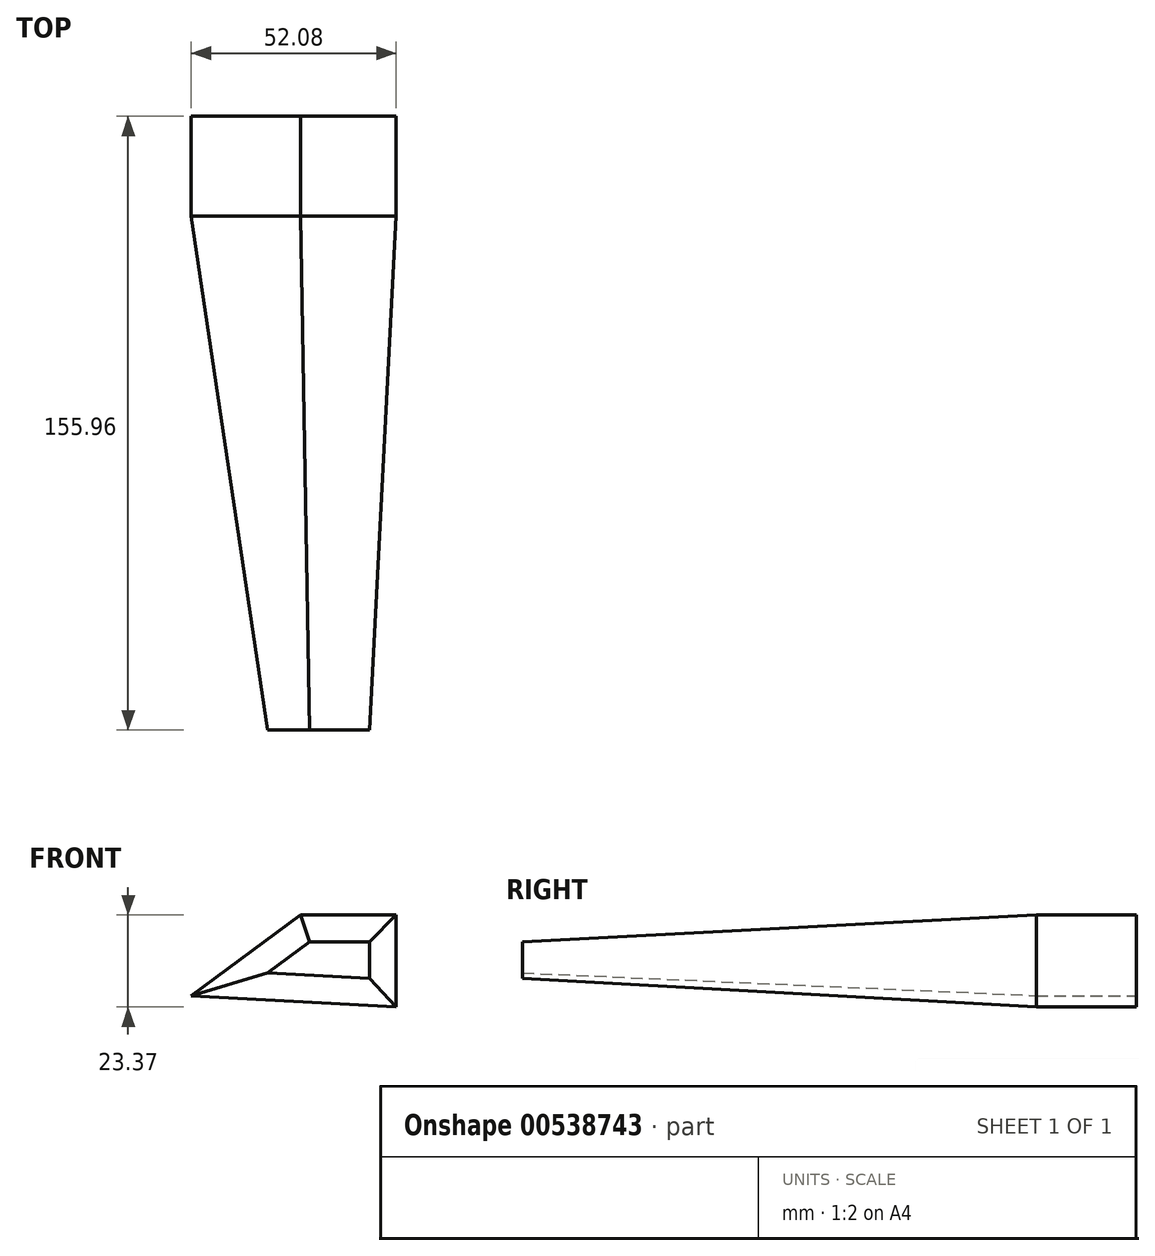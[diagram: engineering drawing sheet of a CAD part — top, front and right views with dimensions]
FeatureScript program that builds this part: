
annotation { "Feature Type Name" : "Feature", "Feature Type Description" : "" }
export const myFeature = defineFeature(function(context is Context, id is Id, definition is map)
    precondition{}
    {
        {
            var Q0;
            Q0=qCreatedBy(makeId("Front.planeOp"),FACE);
            var sketch = newSketch(context, id + "F0", { "sketchPlane" : qUnion([Q0])});
            skLineSegment(sketch, "E0", {"start": v(-63.5, 31.08) * mm, "end": v(-35.69, 51.55) * mm});
            skLineSegment(sketch, "E1", {"start": v(-35.69, 51.55) * mm, "end": v(-11.42, 51.55) * mm});
            skLineSegment(sketch, "E2", {"start": v(-11.42, 51.55) * mm, "end": v(-11.42, 28.18) * mm});
            skLineSegment(sketch, "E3", {"start": v(-11.42, 28.18) * mm, "end": v(-63.5, 31.08) * mm});
            skSolve(sketch);
        }
        {
            var Q0;
            Q0=makeQuery(id+"F0.imprint","IMPRINT",FACE,{"disambiguationData":[TD([[makeQuery(id+"F0.imprint","IMPRINT",EDGE,{"derivedFrom":sQuery(id+"F0.wireOp",EDGE,"E0")}),-1.0]])]});
            var sketch = newSketch(context, id + "F1", { "sketchPlane" : qUnion([Q0])});
            skSolve(sketch);
        }
        {
            var Q0;
            Q0 = qSketchRegion(id + "F1", true);
            var Q1;
            Q1=makeQuery(id+"F0.imprint","IMPRINT",FACE,{"disambiguationData":[TD([[makeQuery(id+"F0.imprint","IMPRINT",EDGE,{"derivedFrom":sQuery(id+"F0.wireOp",EDGE,"E0")}),-1.0]])]});
            extrude(context, id + "F2", {"entities" : qUnion([Q0, Q1]), "depth" : 130.56 * mm, "offsetDistance" : 25.4 * mm, "hasDraft" : true, "draftAngle" : 3 * degree, "draftPullDirection" : true, "hasSecondDirection" : true, "secondDirectionOppositeDirection" : true, "secondDirectionDepth" : 25.4 * mm});
        }
    });
